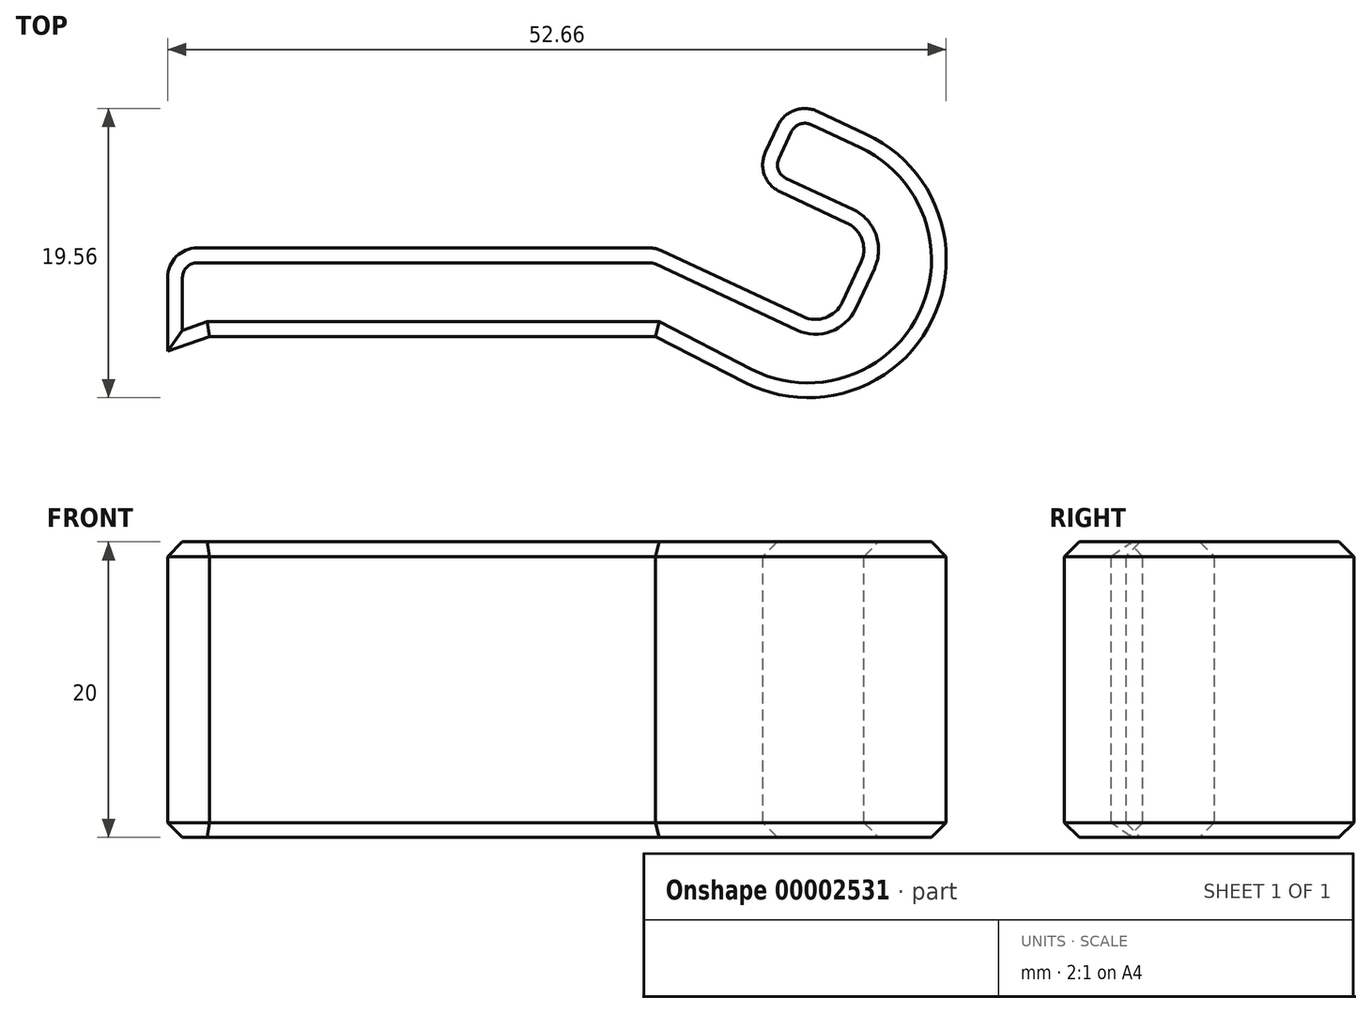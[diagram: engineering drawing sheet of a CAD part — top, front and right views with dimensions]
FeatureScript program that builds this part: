
annotation { "Feature Type Name" : "Feature", "Feature Type Description" : "" }
export const myFeature = defineFeature(function(context is Context, id is Id, definition is map)
    precondition{}
    {
        {
            var Q0;
            Q0=qCreatedBy(makeId("Top.planeOp"),FACE);
            var sketch = newSketch(context, id + "F0", { "sketchPlane" : qUnion([Q0])});
            skLineSegment(sketch, "E0", {"start": v(0, 0) * mm, "end": v(-33, 0) * mm});
            skLineSegment(sketch, "E1", {"start": v(-33, 0) * mm, "end": v(-33, 6) * mm});
            skLineSegment(sketch, "E2", {"start": v(-33, 6) * mm, "end": v(0, 6) * mm});
            skLineSegment(sketch, "E3", {"start": v(0, 6) * mm, "end": v(11.78, 0.5) * mm});
            skLineSegment(sketch, "E4", {"start": v(11.78, 0.5) * mm, "end": v(14.74, 6.85) * mm});
            skLineSegment(sketch, "E5", {"start": v(14.74, 6.85) * mm, "end": v(6.58, 10.65) * mm});
            skLineSegment(sketch, "E6", {"start": v(6.58, 10.65) * mm, "end": v(9.12, 16.1) * mm});
            skLineSegment(sketch, "E7", {"start": v(9.12, 16.1) * mm, "end": v(14.26, 13.7) * mm});
            skLineSegment(sketch, "E8", {"start": v(0, 0) * mm, "end": v(6.04, -3.1) * mm});
            skArc(sketch, "E9", {"start": v(6.04, -3.1) * mm, "mid": v(18.7, 1.1) * mm, "end": v(14.26, 13.7) * mm});
            skLineSegment(sketch, "E10", {"start": v(-33, 0) * mm, "end": v(-33, -1) * mm});
            skLineSegment(sketch, "E11", {"start": v(-33, -1) * mm, "end": v(-30.17, 0) * mm});
            skSolve(sketch);
        }
        {
            var Q0;
            Q0=makeQuery(id+"F0.imprint","IMPRINT",FACE,{"disambiguationData":[TD([[makeQuery(id+"F0.imprint","IMPRINT",EDGE,{"derivedFrom":sQuery(id+"F0.wireOp",EDGE,"E0")}),-1.0]])]});
            var Q1;
            {var subQ0=sQuery(id+"F0.wireOp",EDGE,"a9b59dd7-f27a-40b9-b760-6b068efdd8e0");Q1=makeQuery(id+"F0.imprint","IMPRINT",FACE,{"disambiguationData":[TD([[makeQuery(id+"F0.imprint","IMPRINT",EDGE,{"derivedFrom":subQ0}),1.0]])]});}
            var Q2;
            {var subQ0=sQuery(id+"F0.wireOp",EDGE,"E10");Q2=makeQuery(id+"F0.imprint","IMPRINT",FACE,{"disambiguationData":[TD([[makeQuery(id+"F0.imprint","IMPRINT",EDGE,{"derivedFrom":subQ0}),1.0]])]});}
            extrude(context, id + "F1", {"entities" : qUnion([Q0, Q1, Q2]), "endBound" : BoundingType.SYMMETRIC, "depth" : 20 * mm, "offsetDistance" : 25 * mm});
        }
        {
            var Q0;
            Q0=makeQuery(id+"F1.opExtrude","SWEPT_EDGE",EDGE,{"disambiguationData":[OSD([sQuery(id+"F0.wireOp",EDGE,"E1"),sQuery(id+"F0.wireOp",EDGE,"E2")])]});
            var Q1;
            Q1=makeQuery(id+"F1.opExtrude","SWEPT_EDGE",EDGE,{"disambiguationData":[OSD([sQuery(id+"F0.wireOp",EDGE,"E6"),sQuery(id+"F0.wireOp",EDGE,"E7")])]});
            var Q2;
            Q2=makeQuery(id+"F1.opExtrude","SWEPT_EDGE",EDGE,{"disambiguationData":[OSD([sQuery(id+"F0.wireOp",EDGE,"E5"),sQuery(id+"F0.wireOp",EDGE,"E6")])]});
            var Q3;
            Q3=makeQuery(id+"F1.opExtrude","SWEPT_EDGE",EDGE,{"disambiguationData":[OSD([sQuery(id+"F0.wireOp",EDGE,"E4"),sQuery(id+"F0.wireOp",EDGE,"E5")])]});
            var Q4;
            Q4=makeQuery(id+"F1.opExtrude","SWEPT_EDGE",EDGE,{"disambiguationData":[OSD([sQuery(id+"F0.wireOp",EDGE,"E3"),sQuery(id+"F0.wireOp",EDGE,"E4")])]});
            var Q5;
            Q5=makeQuery(id+"F1.opExtrude","SWEPT_EDGE",EDGE,{"disambiguationData":[OSD([sQuery(id+"F0.wireOp",EDGE,"E2"),sQuery(id+"F0.wireOp",EDGE,"E3")])]});
            fillet(context, id + "F2", {"entities" : qUnion([Q0, Q1, Q2, Q3, Q4, Q5]), "radius" : 2 * mm, "tangentPropagation" : true, "allowEdgeOverflow" : false});
        }
        {
            var Q0;
            Q0=makeQuery(id+"F1.opExtrude","CAP_EDGE",EDGE,{"disambiguationData":[OSD([sQuery(id+"F0.wireOp",EDGE,"E2")])],"isStart":false});
            var Q1;
            Q1=makeQuery(id+"F1.opExtrude","CAP_EDGE",EDGE,{"disambiguationData":[OSD([sQuery(id+"F0.wireOp",EDGE,"E2")])],"isStart":true});
            var Q2;
            Q2=makeQuery(id+"F1.opExtrude","CAP_EDGE",EDGE,{"disambiguationData":[OSD([sQuery(id+"F0.wireOp",EDGE,"E0")])],"isStart":false});
            var Q3;
            Q3=makeQuery(id+"F1.opExtrude","CAP_EDGE",EDGE,{"disambiguationData":[OSD([sQuery(id+"F0.wireOp",EDGE,"E0")])],"isStart":true});
            var Q4;
            Q4=makeQuery(id+"F1.opExtrude","CAP_EDGE",EDGE,{"disambiguationData":[OSD([sQuery(id+"F0.wireOp",EDGE,"E11")])],"isStart":true});
            var Q5;
            Q5=makeQuery(id+"F1.opExtrude","CAP_EDGE",EDGE,{"disambiguationData":[OSD([sQuery(id+"F0.wireOp",EDGE,"E11")])],"isStart":false});
            chamfer(context, id + "F3", {"entities" : qUnion([Q0, Q1, Q2, Q3, Q4, Q5]), "width" : 1 * mm, "tangentPropagation" : true});
        }
    });
